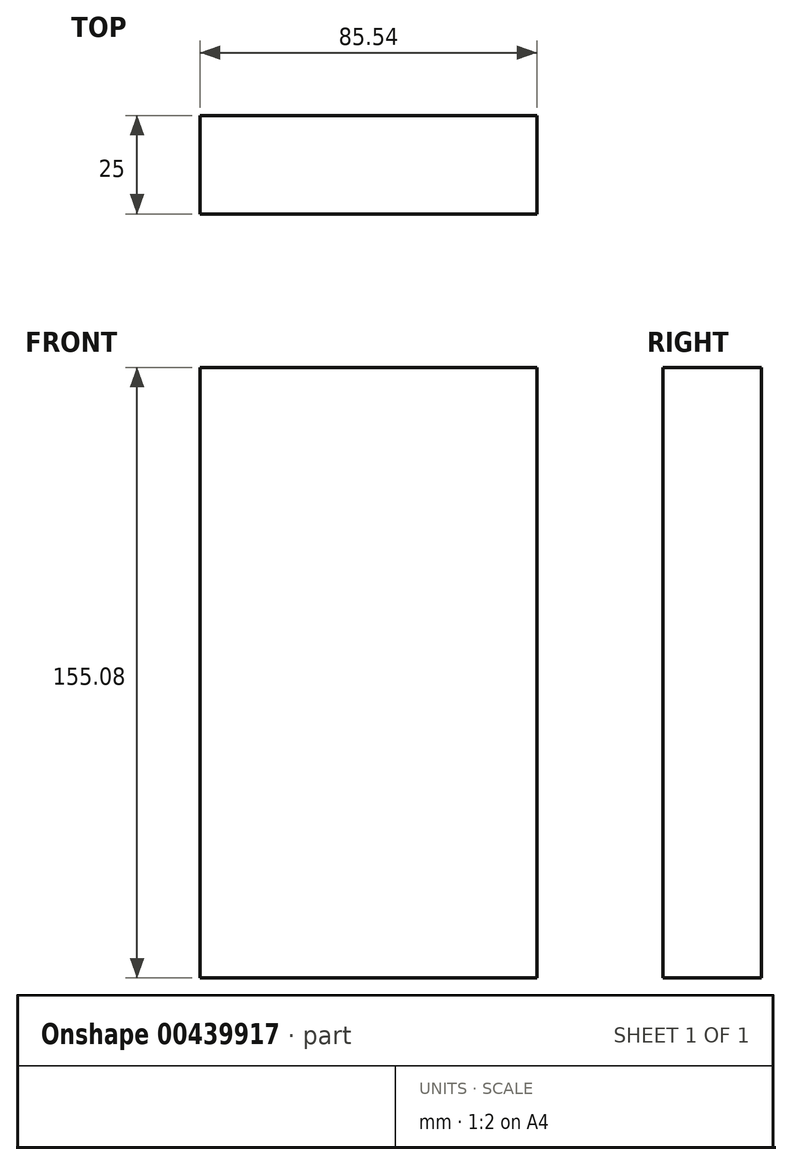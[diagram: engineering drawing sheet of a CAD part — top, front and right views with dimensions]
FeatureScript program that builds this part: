
annotation { "Feature Type Name" : "Feature", "Feature Type Description" : "" }
export const myFeature = defineFeature(function(context is Context, id is Id, definition is map)
    precondition{}
    {
        {
            var Q0;
            Q0=qCreatedBy(makeId("Front.planeOp"),FACE);
            var sketch = newSketch(context, id + "F0", { "sketchPlane" : qUnion([Q0])});
            skLineSegment(sketch, "E0.bottom", {"start": v(42.77, 77.54) * mm, "end": v(-42.77, 77.54) * mm});
            skLineSegment(sketch, "E0.top", {"start": v(42.77, -77.54) * mm, "end": v(-42.77, -77.54) * mm});
            skLineSegment(sketch, "E0.left", {"start": v(42.77, 77.54) * mm, "end": v(42.77, -77.54) * mm});
            skLineSegment(sketch, "E0.right", {"start": v(-42.77, 77.54) * mm, "end": v(-42.77, -77.54) * mm});
            skPoint(sketch, "E0.middle", {"position": v(0, 0) * mm});
            skSolve(sketch);
        }
        {
            var Q0;
            Q0=makeQuery(id+"F0.imprint","IMPRINT",FACE,{"disambiguationData":[TD([[makeQuery(id+"F0.imprint","IMPRINT",EDGE,{"derivedFrom":sQuery(id+"F0.wireOp",EDGE,"E0.bottom")}),1.0]])]});
            extrude(context, id + "F1", {"entities" : qUnion([Q0]), "depth" : 25 * mm});
        }
    });
